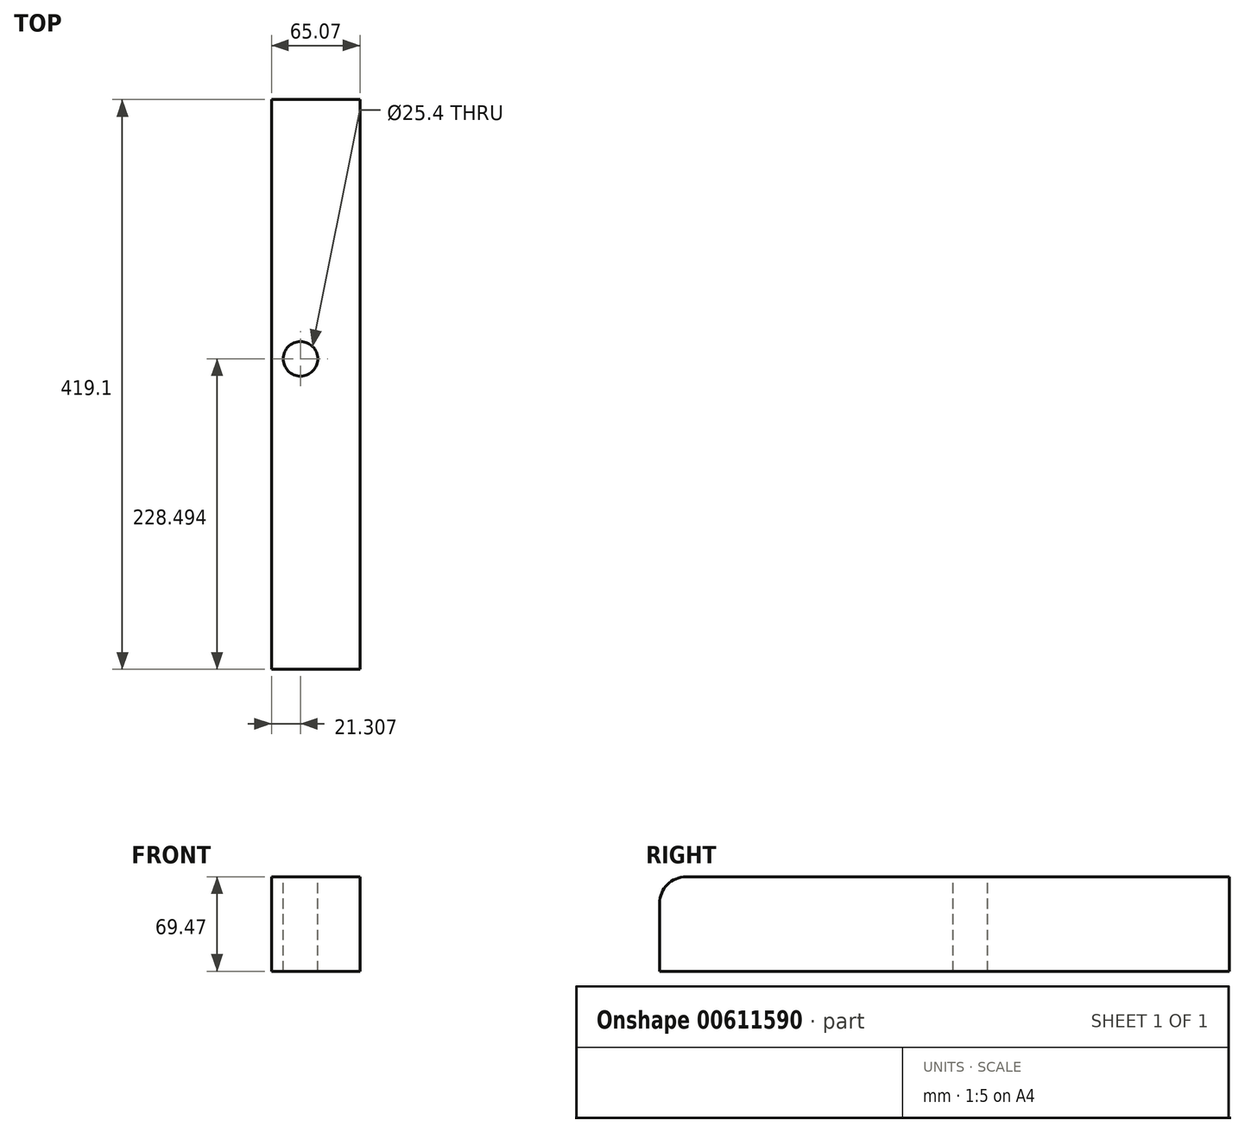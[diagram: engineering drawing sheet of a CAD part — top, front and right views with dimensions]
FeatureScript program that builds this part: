
annotation { "Feature Type Name" : "Feature", "Feature Type Description" : "" }
export const myFeature = defineFeature(function(context is Context, id is Id, definition is map)
    precondition{}
    {
        {
            var Q0;
            Q0=qCreatedBy(makeId("Front.planeOp"),FACE);
            var sketch = newSketch(context, id + "F0", { "sketchPlane" : qUnion([Q0])});
            skLineSegment(sketch, "E0", {"start": v(0, 45.62) * mm, "end": v(0, 115.09) * mm});
            skLineSegment(sketch, "E1", {"start": v(0, 115.09) * mm, "end": v(65.07, 115.09) * mm});
            skLineSegment(sketch, "E2", {"start": v(65.07, 115.09) * mm, "end": v(65.07, 45.62) * mm});
            skLineSegment(sketch, "E3", {"start": v(65.07, 45.62) * mm, "end": v(0, 45.62) * mm});
            skSolve(sketch);
        }
        {
            var Q0;
            Q0=makeQuery(id+"F0.imprint","IMPRINT",FACE,{"disambiguationData":[TD([[makeQuery(id+"F0.imprint","IMPRINT",EDGE,{"derivedFrom":sQuery(id+"F0.wireOp",EDGE,"E0")}),-1.0]])]});
            extrude(context, id + "F1", {"entities" : qUnion([Q0]), "depth" : 419.1 * mm, "offsetDistance" : 25.4 * mm});
        }
        {
            var Q0;
            Q0=makeQuery(id+"F1.opExtrude","CAP_EDGE",EDGE,{"disambiguationData":[OSD([sQuery(id+"F0.wireOp",EDGE,"E1")])],"isStart":false});
            fillet(context, id + "F2", {"entities" : qUnion([Q0]), "radius" : 19.62 * mm, "tangentPropagation" : true, "allowEdgeOverflow" : false});
        }
        {
            var Q0;
            Q0=makeQuery(id+"F1.opExtrude","SWEPT_FACE",FACE,{"disambiguationData":[OSD([sQuery(id+"F0.wireOp",EDGE,"E1")])]});
            var sketch = newSketch(context, id + "F3", { "sketchPlane" : qUnion([Q0])});
            skPoint(sketch, "E4", {"position": v(21.3, -190.6) * mm});
            skSolve(sketch);
        }
        {
            var Q0;
            Q0=sQuery(id+"F3.wireOp",VERTEX,"E4");
            var Q1;
            Q1=makeQuery(id+"F1.opExtrude","SWEPT_BODY",BODY,{"disambiguationData":[OSD([sQuery(id+"F0.wireOp",EDGE,"E0"),sQuery(id+"F0.wireOp",EDGE,"E1"),sQuery(id+"F0.wireOp",EDGE,"E2"),sQuery(id+"F0.wireOp",EDGE,"E3")])]});
            hole(context, id + "F4", {"style" : HoleStyle.SIMPLE, "endStyle" : HoleEndStyle.THROUGH, "holeDiameter" : 25.4 * mm, "majorDiameter" : 6.35 * mm, "isTappedThrough" : true, "tappedDepth" : 12.7 * mm, "tapClearance" : 3, "locations" : qUnion([Q0]), "scope" : qUnion([Q1])});
        }
    });
